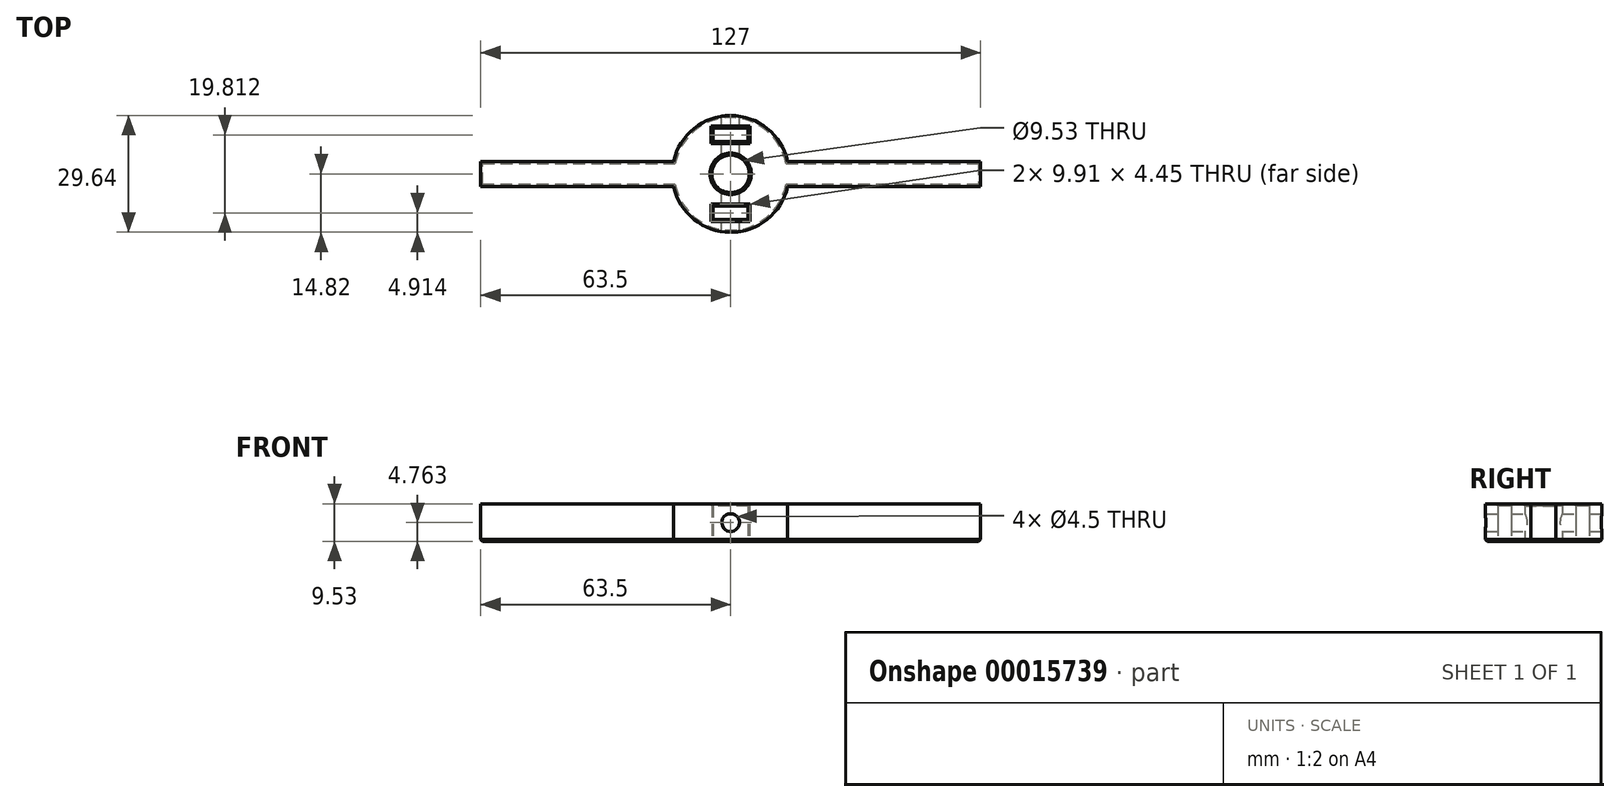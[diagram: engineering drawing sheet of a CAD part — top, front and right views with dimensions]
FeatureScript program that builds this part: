
annotation { "Feature Type Name" : "Feature", "Feature Type Description" : "" }
export const myFeature = defineFeature(function(context is Context, id is Id, definition is map)
    precondition{}
    {
        {
            var Q0;
            Q0=qCreatedBy(makeId("Top.planeOp"),FACE);
            var sketch = newSketch(context, id + "F0", { "sketchPlane" : qUnion([Q0])});
            skCircle(sketch, "E0", {"center": v(0, 0) * mm, "radius": 4.76 * mm});
            skLineSegment(sketch, "E1", {"start": v(-14.48, 0) * mm, "end": v(14.48, 0) * mm, "construction": true});
            skLineSegment(sketch, "E2.bottom", {"start": v(14.48, 3.18) * mm, "end": v(63.5, 3.18) * mm});
            skLineSegment(sketch, "E2.top", {"start": v(14.48, -3.17) * mm, "end": v(63.5, -3.17) * mm});
            skLineSegment(sketch, "E2.left", {"start": v(14.48, 3.18) * mm, "end": v(14.48, -3.18) * mm});
            skLineSegment(sketch, "E2.right", {"start": v(63.5, 3.17) * mm, "end": v(63.5, -3.17) * mm});
            skLineSegment(sketch, "E3.bottom", {"start": v(-14.48, 3.18) * mm, "end": v(-63.5, 3.18) * mm});
            skLineSegment(sketch, "E3.top", {"start": v(-14.48, -3.17) * mm, "end": v(-63.5, -3.17) * mm});
            skLineSegment(sketch, "E3.left", {"start": v(-14.48, 3.18) * mm, "end": v(-14.48, -3.18) * mm});
            skLineSegment(sketch, "E3.right", {"start": v(-63.5, 3.17) * mm, "end": v(-63.5, -3.17) * mm});
            skLineSegment(sketch, "E4", {"start": v(0, 4.76) * mm, "end": v(0, -4.76) * mm, "construction": true});
            skLineSegment(sketch, "E5", {"start": v(0, -4.76) * mm, "end": v(0, -8.2) * mm, "construction": true});
            skLineSegment(sketch, "E6", {"start": v(0, 4.76) * mm, "end": v(0, 8.2) * mm, "construction": true});
            skLineSegment(sketch, "E7.bottom", {"start": v(-4.44, 11.62) * mm, "end": v(4.44, 11.62) * mm});
            skLineSegment(sketch, "E7.top", {"start": v(-4.44, 8.2) * mm, "end": v(4.44, 8.2) * mm});
            skLineSegment(sketch, "E7.left", {"start": v(-4.44, 11.62) * mm, "end": v(-4.44, 8.2) * mm});
            skLineSegment(sketch, "E7.right", {"start": v(4.44, 11.62) * mm, "end": v(4.44, 8.2) * mm});
            skLineSegment(sketch, "E8.bottom", {"start": v(-4.44, -8.2) * mm, "end": v(4.44, -8.2) * mm});
            skLineSegment(sketch, "E8.top", {"start": v(-4.45, -11.62) * mm, "end": v(4.45, -11.62) * mm});
            skLineSegment(sketch, "E8.left", {"start": v(-4.44, -8.2) * mm, "end": v(-4.44, -11.62) * mm});
            skLineSegment(sketch, "E8.right", {"start": v(4.45, -8.2) * mm, "end": v(4.45, -11.62) * mm});
            skCircle(sketch, "E9", {"center": v(4.44, 11.62) * mm, "radius": 2.38 * mm, "construction": true});
            skArc(sketch, "E10", {"start": v(14.48, 3.18) * mm, "mid": v(0, 14.82) * mm, "end": v(-14.48, 3.18) * mm});
            skArc(sketch, "E11", {"start": v(-14.48, -3.18) * mm, "mid": v(0, -14.82) * mm, "end": v(14.48, -3.18) * mm});
            skSolve(sketch);
        }
        {
            var Q0;
            Q0 = qSketchRegion(id + "F0", true);
            extrude(context, id + "F1", {"entities" : qUnion([Q0]), "depth" : 9.52 * mm});
        }
        {
            var Q0;
            Q0=makeQuery(id+"F1.opExtrude","SWEPT_FACE",FACE,{"disambiguationData":[OSD([sQuery(id+"F0.wireOp",EDGE,"E8.bottom")])]});
            var sketch = newSketch(context, id + "F2", { "sketchPlane" : qUnion([Q0])});
            skLineSegment(sketch, "E12", {"start": v(0, 9.53) * mm, "end": v(0, 0) * mm, "construction": true});
            skCircle(sketch, "E13", {"center": v(0, 4.76) * mm, "radius": 2.25 * mm});
            skSolve(sketch);
        }
        {
            var Q0;
            Q0 = qSketchRegion(id + "F2", true);
            var Q1;
            Q1=makeQuery(id+"F1.opExtrude","SWEPT_FACE",FACE,{"disambiguationData":[OSD([sQuery(id+"F0.wireOp",EDGE,"E11")])]});
            var Q2;
            Q2=makeQuery(id+"F1.opExtrude","SWEPT_FACE",FACE,{"disambiguationData":[OSD([sQuery(id+"F0.wireOp",EDGE,"E10")])]});
            extrude(context, id + "F3", {"entities" : qUnion([Q0]), "operationType" : NewBodyOperationType.REMOVE, "endBound" : BoundingType.UP_TO_SURFACE, "endBoundEntityFace" : qUnion([Q1]), "depth" : 25.4 * mm, "hasSecondDirection" : true, "secondDirectionBound" : BoundingType.UP_TO_SURFACE, "secondDirectionOppositeDirection" : true, "secondDirectionBoundEntityFace" : qUnion([Q2]), "secondDirectionDepth" : 25.4 * mm});
        }
        {
            var Q0;
            Q0=makeQuery(id+"F1.opExtrude","CAP_FACE",FACE,{"disambiguationData":[OSD([sQuery(id+"F0.wireOp",EDGE,"E0"),sQuery(id+"F0.wireOp",EDGE,"E2.bottom"),sQuery(id+"F0.wireOp",EDGE,"E2.top"),sQuery(id+"F0.wireOp",EDGE,"E2.right"),sQuery(id+"F0.wireOp",EDGE,"E3.bottom"),sQuery(id+"F0.wireOp",EDGE,"E3.top"),sQuery(id+"F0.wireOp",EDGE,"E3.right"),sQuery(id+"F0.wireOp",EDGE,"E7.bottom"),sQuery(id+"F0.wireOp",EDGE,"E7.top"),sQuery(id+"F0.wireOp",EDGE,"E7.left"),sQuery(id+"F0.wireOp",EDGE,"E7.right"),sQuery(id+"F0.wireOp",EDGE,"E8.bottom"),sQuery(id+"F0.wireOp",EDGE,"E8.top"),sQuery(id+"F0.wireOp",EDGE,"E8.left"),sQuery(id+"F0.wireOp",EDGE,"E8.right"),sQuery(id+"F0.wireOp",EDGE,"E10"),sQuery(id+"F0.wireOp",EDGE,"E11")])],"isStart":true});
            chamfer(context, id + "F4", {"entities" : qUnion([Q0]), "width" : 0.5 * mm});
        }
        {
            var Q0;
            Q0=makeQuery(id+"F1.opExtrude","CAP_EDGE",EDGE,{"disambiguationData":[OSD([sQuery(id+"F0.wireOp",EDGE,"E7.left")])],"isStart":false});
            var Q1;
            Q1=makeQuery(id+"F1.opExtrude","CAP_EDGE",EDGE,{"disambiguationData":[OSD([sQuery(id+"F0.wireOp",EDGE,"E7.bottom")])],"isStart":false});
            var Q2;
            Q2=makeQuery(id+"F1.opExtrude","CAP_EDGE",EDGE,{"disambiguationData":[OSD([sQuery(id+"F0.wireOp",EDGE,"E7.right")])],"isStart":false});
            var Q3;
            Q3=makeQuery(id+"F1.opExtrude","CAP_EDGE",EDGE,{"disambiguationData":[OSD([sQuery(id+"F0.wireOp",EDGE,"E7.top")])],"isStart":false});
            var Q4;
            Q4=makeQuery(id+"F1.opExtrude","CAP_EDGE",EDGE,{"disambiguationData":[OSD([sQuery(id+"F0.wireOp",EDGE,"E8.bottom")])],"isStart":false});
            var Q5;
            Q5=makeQuery(id+"F1.opExtrude","CAP_EDGE",EDGE,{"disambiguationData":[OSD([sQuery(id+"F0.wireOp",EDGE,"E8.right")])],"isStart":false});
            var Q6;
            Q6=makeQuery(id+"F1.opExtrude","CAP_EDGE",EDGE,{"disambiguationData":[OSD([sQuery(id+"F0.wireOp",EDGE,"E8.top")])],"isStart":false});
            var Q7;
            Q7=makeQuery(id+"F1.opExtrude","CAP_EDGE",EDGE,{"disambiguationData":[OSD([sQuery(id+"F0.wireOp",EDGE,"E8.left")])],"isStart":false});
            var Q8;
            Q8=makeQuery(id+"F1.opExtrude","CAP_EDGE",EDGE,{"disambiguationData":[OSD([sQuery(id+"F0.wireOp",EDGE,"E0")])],"isStart":false});
            chamfer(context, id + "F5", {"entities" : qUnion([Q0, Q1, Q2, Q3, Q4, Q5, Q6, Q7, Q8]), "width" : 0.5 * mm, "tangentPropagation" : true});
        }
    });
